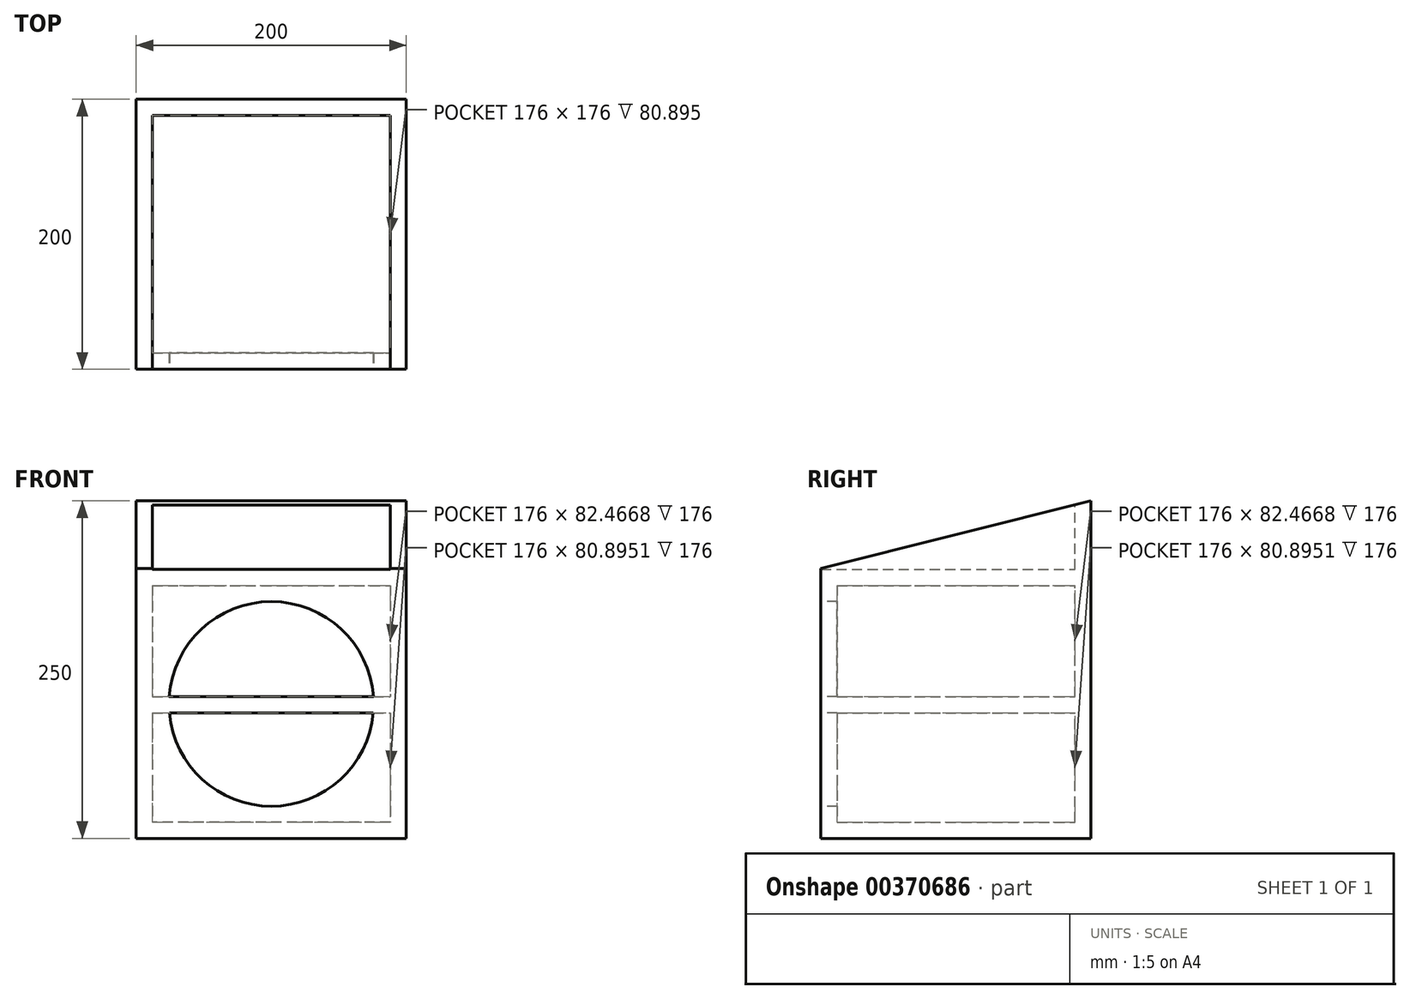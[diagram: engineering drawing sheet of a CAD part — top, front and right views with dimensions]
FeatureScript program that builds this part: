
annotation { "Feature Type Name" : "Feature", "Feature Type Description" : "" }
export const myFeature = defineFeature(function(context is Context, id is Id, definition is map)
    precondition{}
    {
        {
            var Q0;
            Q0=qCreatedBy(makeId("Right.planeOp"),FACE);
            var sketch = newSketch(context, id + "F0", { "sketchPlane" : qUnion([Q0])});
            skLineSegment(sketch, "E0", {"start": v(-124.5, -124.93) * mm, "end": v(75.5, -124.93) * mm});
            skLineSegment(sketch, "E1", {"start": v(75.5, -124.93) * mm, "end": v(75.5, 125.07) * mm});
            skLineSegment(sketch, "E2", {"start": v(75.5, 125.07) * mm, "end": v(-124.5, 75.07) * mm});
            skLineSegment(sketch, "E3", {"start": v(-124.5, 75.07) * mm, "end": v(-124.5, -124.93) * mm});
            skSolve(sketch);
        }
        {
            var Q0;
            Q0=makeQuery(id+"F0.imprint","IMPRINT",FACE,{"disambiguationData":[TD([[makeQuery(id+"F0.imprint","IMPRINT",EDGE,{"derivedFrom":sQuery(id+"F0.wireOp",EDGE,"E0")}),1.0]])]});
            extrude(context, id + "F1", {"entities" : qUnion([Q0]), "endBound" : BoundingType.SYMMETRIC, "depth" : 200 * mm});
        }
        {
            var Q0;
            Q0=makeQuery(id+"F1.opExtrude","SWEPT_FACE",FACE,{"disambiguationData":[OSD([sQuery(id+"F0.wireOp",EDGE,"E3")])]});
            var Q1;
            Q1=makeQuery(id+"F1.opExtrude","SWEPT_FACE",FACE,{"disambiguationData":[OSD([sQuery(id+"F0.wireOp",EDGE,"E2")])]});
            shell(context, id + "F2", {"entities" : qUnion([Q0, Q1]), "thickness" : 12 * mm});
        }
        {
            var Q0;
            Q0=makeQuery(id+"F2.opShell","OFFSET_FACE",FACE,{"disambiguationData":[OSD([sQuery(id+"F0.wireOp",EDGE,"E1")])]});
            var sketch = newSketch(context, id + "F3", { "sketchPlane" : qUnion([Q0])});
            skLineSegment(sketch, "E4.bottom", {"start": v(-88.3, 74.43) * mm, "end": v(88, 74.43) * mm});
            skLineSegment(sketch, "E4.top", {"start": v(-88.3, 62.43) * mm, "end": v(88, 62.43) * mm});
            skLineSegment(sketch, "E4.left", {"start": v(-88.3, 74.43) * mm, "end": v(-88.3, 62.43) * mm});
            skLineSegment(sketch, "E4.right", {"start": v(88, 74.43) * mm, "end": v(88, 62.43) * mm});
            skLineSegment(sketch, "E5.bottom", {"start": v(-97.53, -20.03) * mm, "end": v(97.53, -20.03) * mm});
            skLineSegment(sketch, "E5.top", {"start": v(-97.53, -32.03) * mm, "end": v(97.53, -32.03) * mm});
            skLineSegment(sketch, "E5.left", {"start": v(-97.53, -20.03) * mm, "end": v(-97.53, -32.03) * mm});
            skLineSegment(sketch, "E5.right", {"start": v(97.53, -20.03) * mm, "end": v(97.53, -32.03) * mm});
            skPoint(sketch, "E5.middle", {"position": v(0, -26.03) * mm});
            skSolve(sketch);
        }
        {
            var Q0;
            {var subQ0=sQuery(id+"F3.wireOp",EDGE,"E5.bottom");var subQ1=sQuery(id+"F0.wireOp",EDGE,"E1");var subQ2=makeQuery(id+"F2.opShell","OFFSET_EDGE",EDGE,{"disambiguationData":[OSD([subQ1]),TDD([makeQuery(id+"F1.opExtrude","CAP_EDGE",EDGE,{"disambiguationData":[OSD([subQ1])],"isStart":true})])]});var subQ3=makeQuery(id+"F3.imprint","INTERSECT",VERTEX,{"derivedFrom":[subQ2,subQ0]});Q0=makeQuery(id+"F3.imprint","IMPRINT",FACE,{"disambiguationData":[TD([[makeQuery(id+"F3.imprint","IMPRINT",EDGE,{"disambiguationData":[TD([[subQ3,-1.0]])],"derivedFrom":subQ0}),-1.0]])]});}
            var Q1;
            {var subQ0=sQuery(id+"F3.wireOp",EDGE,"E4.right");Q1=makeQuery(id+"F3.imprint","IMPRINT",FACE,{"disambiguationData":[TD([[makeQuery(id+"F3.imprint","IMPRINT",EDGE,{"derivedFrom":subQ0}),1.0]])]});}
            extrude(context, id + "F4", {"entities" : qUnion([Q0, Q1]), "operationType" : NewBodyOperationType.ADD, "depth" : 188 * mm});
        }
        {
            var Q0;
            {var subQ0=sQuery(id+"F0.wireOp",EDGE,"E1");Q0=makeQuery(id+"F4.boolean.opBoolean","MERGE",FACE,{"derivedFrom":[makeQuery(id+"F1.opExtrude","SWEPT_FACE",FACE,{"disambiguationData":[OSD([sQuery(id+"F0.wireOp",EDGE,"E3")])]}),makeQuery(id+"F4.opExtrude","CAP_FACE",FACE,{"disambiguationData":[OSD([subQ0,sQuery(id+"F3.wireOp",EDGE,"E4.bottom"),sQuery(id+"F3.wireOp",EDGE,"E4.top"),sQuery(id+"F3.wireOp",EDGE,"E4.right")])],"isStart":false}),makeQuery(id+"F4.opExtrude","CAP_FACE",FACE,{"disambiguationData":[OSD([subQ0,sQuery(id+"F3.wireOp",EDGE,"E5.bottom"),sQuery(id+"F3.wireOp",EDGE,"E5.top")])],"isStart":false})]});}
            var sketch = newSketch(context, id + "F5", { "sketchPlane" : qUnion([Q0])});
            skLineSegment(sketch, "E6.bottom", {"start": v(-88, -112.93) * mm, "end": v(88, -112.93) * mm});
            skLineSegment(sketch, "E6.top", {"start": v(-88, 62.43) * mm, "end": v(88, 62.43) * mm});
            skLineSegment(sketch, "E6.left", {"start": v(-88, -112.93) * mm, "end": v(-88, 62.43) * mm});
            skLineSegment(sketch, "E6.right", {"start": v(88, -112.93) * mm, "end": v(88, 62.43) * mm});
            skCircle(sketch, "E7", {"center": v(0, -25.3) * mm, "radius": 75.8 * mm});
            skPoint(sketch, "E7.centerSnap0", {"position": v(0, -20.03) * mm});
            skSolve(sketch);
        }
        {
            var Q0;
            {var subQ5=sQuery(id+"F5.wireOp",EDGE,"E6.top");Q0=makeQuery(id+"F5.imprint","IMPRINT",FACE,{"disambiguationData":[TD([[makeQuery(id+"F5.imprint","IMPRINT",EDGE,{"derivedFrom":subQ5}),-1.0]])]});}
            var Q1;
            {var subQ1=sQuery(id+"F5.wireOp",EDGE,"E6.bottom");Q1=makeQuery(id+"F5.imprint","IMPRINT",FACE,{"disambiguationData":[TD([[makeQuery(id+"F5.imprint","IMPRINT",EDGE,{"derivedFrom":subQ1}),-1.0]])]});}
            extrude(context, id + "F6", {"entities" : qUnion([Q0, Q1]), "operationType" : NewBodyOperationType.ADD, "oppositeDirection" : true, "depth" : 12 * mm});
        }
    });
